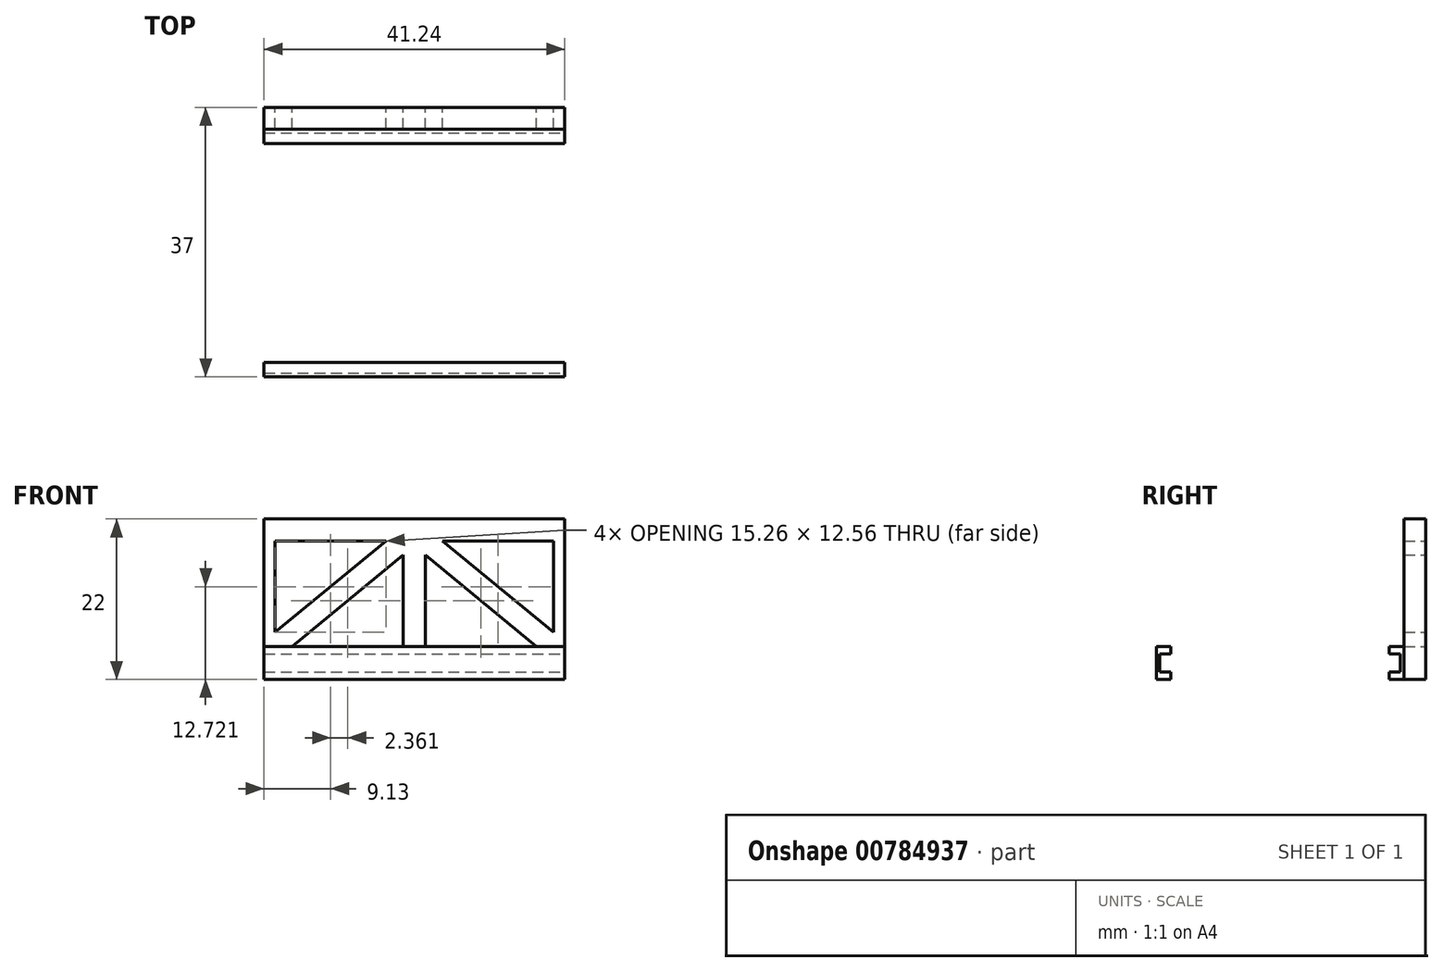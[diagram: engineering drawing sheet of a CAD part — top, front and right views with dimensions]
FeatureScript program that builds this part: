
annotation { "Feature Type Name" : "Feature", "Feature Type Description" : "" }
export const myFeature = defineFeature(function(context is Context, id is Id, definition is map)
    precondition{}
    {
        {
            var Q0;
            Q0=qCreatedBy(makeId("Front.planeOp"),FACE);
            var sketch = newSketch(context, id + "F0", { "sketchPlane" : qUnion([Q0])});
            skLineSegment(sketch, "E0", {"start": v(0, 0) * mm, "end": v(41.24, 0) * mm});
            skLineSegment(sketch, "E1", {"start": v(41.24, 0) * mm, "end": v(41.24, 22) * mm});
            skLineSegment(sketch, "E2", {"start": v(41.24, 22) * mm, "end": v(0, 22) * mm});
            skLineSegment(sketch, "E3", {"start": v(0, 22) * mm, "end": v(0, 0) * mm});
            skLineSegment(sketch, "E4", {"start": v(1.5, 19) * mm, "end": v(16.76, 19) * mm});
            skLineSegment(sketch, "E5", {"start": v(39.74, 19) * mm, "end": v(39.74, 6.44) * mm});
            skLineSegment(sketch, "E6", {"start": v(37.38, 4.5) * mm, "end": v(22.12, 4.5) * mm});
            skLineSegment(sketch, "E7", {"start": v(1.5, 6.44) * mm, "end": v(1.5, 19) * mm});
            skLineSegment(sketch, "E8", {"start": v(19.12, 17.06) * mm, "end": v(19.12, 4.5) * mm});
            skLineSegment(sketch, "E9", {"start": v(22.12, 17.06) * mm, "end": v(22.12, 4.5) * mm});
            skLineSegment(sketch, "E10", {"start": v(1.5, 6.44) * mm, "end": v(16.76, 19) * mm});
            skLineSegment(sketch, "E11", {"start": v(3.86, 4.5) * mm, "end": v(19.12, 17.06) * mm});
            skLineSegment(sketch, "E12", {"start": v(39.74, 6.44) * mm, "end": v(24.48, 19) * mm});
            skLineSegment(sketch, "E13", {"start": v(37.38, 4.5) * mm, "end": v(22.12, 17.06) * mm});
            skLineSegment(sketch, "E14", {"start": v(20.62, 22) * mm, "end": v(20.62, 0) * mm, "construction": true});
            skLineSegment(sketch, "E15", {"start": v(1.5, 4.5) * mm, "end": v(19.12, 19) * mm, "construction": true});
            skLineSegment(sketch, "E16", {"start": v(22.12, 19) * mm, "end": v(39.74, 4.5) * mm, "construction": true});
            skLineSegment(sketch, "E17.trimOffspring", {"start": v(24.48, 19) * mm, "end": v(39.74, 19) * mm});
            skLineSegment(sketch, "E18.trimOffspring", {"start": v(19.12, 4.5) * mm, "end": v(3.86, 4.5) * mm});
            skSolve(sketch);
        }
        {
            var Q0;
            Q0=makeQuery(id+"F0.imprint","IMPRINT",FACE,{"disambiguationData":[TD([[makeQuery(id+"F0.imprint","IMPRINT",EDGE,{"derivedFrom":sQuery(id+"F0.wireOp",EDGE,"E0")}),1.0]])]});
            extrude(context, id + "F1", {"entities" : qUnion([Q0]), "depth" : (3) * mm, "offsetDistance" : 25 * mm});
        }
        {
            var Q0;
            Q0=makeQuery(id+"F1.opExtrude","SWEPT_FACE",FACE,{"disambiguationData":[OSD([sQuery(id+"F0.wireOp",EDGE,"E1")])]});
            var sketch = newSketch(context, id + "F2", { "sketchPlane" : qUnion([Q0])});
            skLineSegment(sketch, "E19", {"start": v(-3, 0) * mm, "end": v(-5, 0) * mm});
            skLineSegment(sketch, "E20", {"start": v(-5, 0) * mm, "end": v(-5, 1) * mm});
            skLineSegment(sketch, "E21", {"start": v(-5, 1) * mm, "end": v(-3.5, 1) * mm});
            skLineSegment(sketch, "E22", {"start": v(-3.5, 1) * mm, "end": v(-3.5, 3.5) * mm});
            skLineSegment(sketch, "E23", {"start": v(-3.5, 3.5) * mm, "end": v(-5, 3.5) * mm});
            skLineSegment(sketch, "E24", {"start": v(-5, 3.5) * mm, "end": v(-5, 4.5) * mm});
            skLineSegment(sketch, "E25", {"start": v(-5, 4.5) * mm, "end": v(-3, 4.5) * mm});
            skSolve(sketch);
        }
        {
            var Q0;
            {var subQ0=sQuery(id+"F2.wireOp",EDGE,"E19");Q0=makeQuery(id+"F2.imprint","IMPRINT",FACE,{"disambiguationData":[TD([[makeQuery(id+"F2.imprint","IMPRINT",EDGE,{"derivedFrom":subQ0}),-1.0]])]});}
            var Q1;
            Q1=makeQuery(id+"F1.opExtrude","SWEPT_FACE",FACE,{"disambiguationData":[OSD([sQuery(id+"F0.wireOp",EDGE,"E3")])]});
            extrude(context, id + "F3", {"entities" : qUnion([Q0]), "endBound" : BoundingType.UP_TO_SURFACE, "oppositeDirection" : true, "depth" : 25 * mm, "endBoundEntityFace" : qUnion([Q1]), "offsetDistance" : 25 * mm});
        }
        {
            var Q0;
            Q0=qCreatedBy(makeId("Front.planeOp"),FACE);
            cPlane(context, id + "F4", {"entities" : qUnion([Q0]), "cplaneType" : CPlaneType.OFFSET, "offset" : 20 * mm, "width" : 150 * mm, "height" : 150 * mm});
        }
        {
            var Q0;
            Q0=makeQuery(id+"F3.opExtrude","SWEPT_BODY",BODY,{"disambiguationData":[OSD([sQuery(id+"F0.wireOp",EDGE,"E1"),sQuery(id+"F2.wireOp",EDGE,"E19"),sQuery(id+"F2.wireOp",EDGE,"E20"),sQuery(id+"F2.wireOp",EDGE,"E21"),sQuery(id+"F2.wireOp",EDGE,"E22"),sQuery(id+"F2.wireOp",EDGE,"E23"),sQuery(id+"F2.wireOp",EDGE,"E24"),sQuery(id+"F2.wireOp",EDGE,"E25")])]});
            var Q1;
            Q1=qCreatedBy(id+"F4.planeOp",FACE);
            mirror(context, id + "F5", {"entities" : qUnion([Q0]), "mirrorPlane" : qUnion([Q1])});
        }
    });
